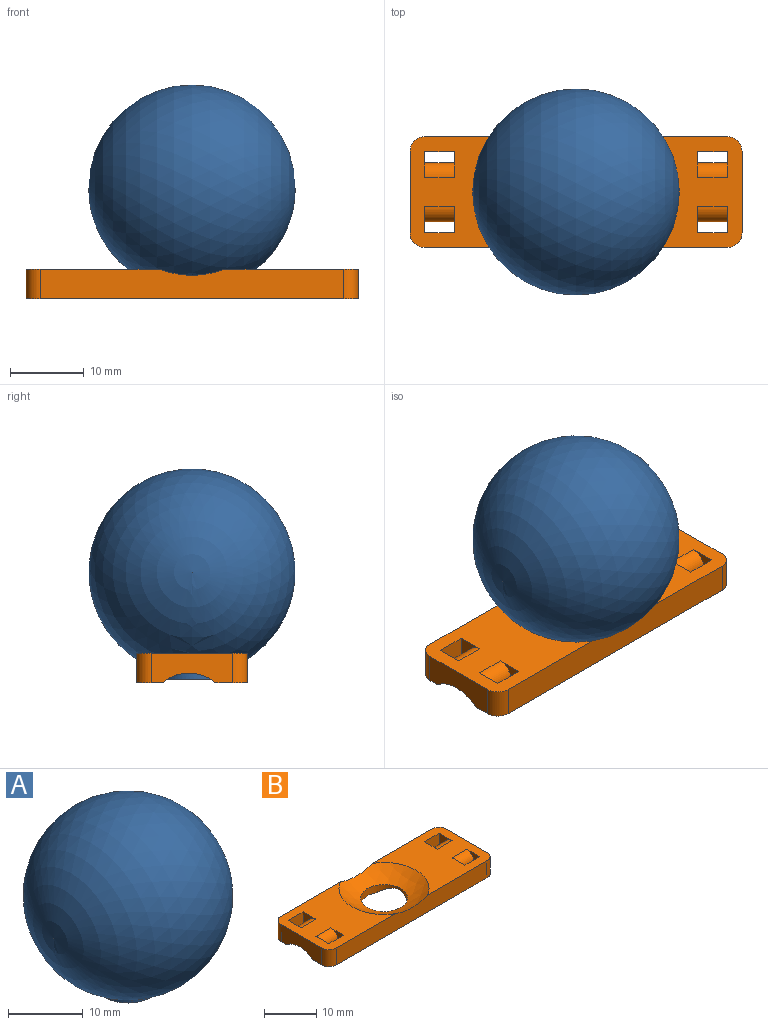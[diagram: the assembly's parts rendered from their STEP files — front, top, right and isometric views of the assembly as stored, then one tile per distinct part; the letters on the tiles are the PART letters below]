
ASSEMBLY  parts=2 mates=1
PART A: 3 faces, bbox 28x28x28.5 mm
  f0: sphere r=14mm, area 2402.1mm2, adj f1
  f1: cylinder r=4.35mm len=8.7mm, axis (0,0,1), area 32.6mm2, adj f0,f2
  f2: plane 8.7x8.7mm, normal (0,0,-1), area 59.4mm2, adj f1
PART B: 36 faces, bbox 45x15.8x5.9 mm
  f0: plane 45x4.26mm, normal (0,0,-1), area 172.5mm2, adj f1,f6,f7,f9,f14,f15,f16,f17
  f1: plane 11x4mm, normal (-1,0,0), area 37.5mm2, adj f0,f2,f3,f32,f33,f34
  f2: plane 18.17x15mm, normal (0,0,1), area 196.8mm2, adj f1,f5,f6,f8,f18,f19,f20,f22
  f3: plane 45x3.43mm, normal (0,0,-1), area 139.9mm2, adj f1,f7,f8,f9,f11,f12,f13,f22
  f4: plane 18.17x15mm, normal (0,0,1), area 196.8mm2, adj f5,f6,f7,f8,f11,f12,f13,f14
  f5: sphere r=14mm, area 181.8mm2, adj f2,f4,f6,f8,f9
  f6: plane 41x4mm, normal (0,-1,0), area 159.2mm2, adj f0,f2,f4,f5,f30,f33
  f7: plane 11x4mm, normal (1,0,0), area 37.5mm2, adj f0,f3,f4,f30,f31,f35
  f8: plane 41x4mm, normal (0,1,0), area 159.2mm2, adj f2,f3,f4,f5,f31,f32
  f9: cylinder r=4.5mm len=9mm, axis (0,0,1), area 35mm2, adj f0,f3,f5,f34,f35
  f10: plane 4x1.94mm, normal (0,1,0), area 7.8mm2, adj f11,f13,f29,f35
  f11: plane 4x3.5mm, normal (1,0,0), area 6.9mm2, adj f3,f4,f10,f12,f29,f35
  f12: plane 4x4mm, normal (0,-1,0), area 16mm2, adj f3,f4,f11,f13
  f13: plane 4x3.5mm, normal (-1,0,0), area 6.9mm2, adj f3,f4,f10,f12,f29,f35
  f14: plane 4x3.5mm, normal (1,0,0), area 6.9mm2, adj f0,f4,f15,f17,f28
  f15: plane 4x2mm, normal (0,-1,0), area 8mm2, adj f0,f14,f16,f28
  f16: plane 4x3.5mm, normal (-1,0,0), area 6.9mm2, adj f0,f4,f15,f17,f28
  f17: plane 4x4mm, normal (0,1,0), area 16mm2, adj f0,f4,f14,f16
  f18: plane 4x3.5mm, normal (-1,0,0), area 6.9mm2, adj f0,f2,f19,f21,f27
  f19: plane 4x4mm, normal (0,1,0), area 16mm2, adj f0,f2,f18,f20
  f20: plane 4x3.5mm, normal (1,0,0), area 6.9mm2, adj f0,f2,f19,f21,f27
  f21: plane 4x2mm, normal (0,-1,0), area 8mm2, adj f0,f18,f20,f27
  f22: plane 4x3.5mm, normal (-1,0,0), area 6.9mm2, adj f2,f3,f23,f25,f26,f34
  f23: plane 4x1.94mm, normal (0,1,0), area 7.8mm2, adj f22,f24,f26,f34
  f24: plane 4x3.5mm, normal (1,0,0), area 6.9mm2, adj f2,f3,f23,f25,f26,f34
  f25: plane 4x4mm, normal (0,-1,0), area 16mm2, adj f2,f3,f22,f24
  f26: cylinder r=2mm len=4mm, axis (-1,0,0), area 12.6mm2, adj f2,f22,f23,f24
  f27: cylinder r=2mm len=4mm, axis (1,0,0), area 12.6mm2, adj f2,f18,f20,f21
  f28: cylinder r=2mm len=4mm, axis (1,0,0), area 12.6mm2, adj f4,f14,f15,f16
  f29: cylinder r=2mm len=4mm, axis (-1,0,0), area 12.6mm2, adj f4,f10,f11,f13
  f30: cylinder r=2mm len=4mm, axis (0,0,-1), area 12.6mm2, adj f0,f4,f6,f7
  f31: cylinder r=2mm len=4mm, axis (0,0,1), area 12.6mm2, adj f3,f4,f7,f8
  f32: cylinder r=2mm len=4mm, axis (0,0,-1), area 12.6mm2, adj f1,f2,f3,f8
  f33: cylinder r=2mm len=4mm, axis (0,0,1), area 12.6mm2, adj f0,f1,f2,f6
  f34: cylinder r=5.8mm len=20.59mm, axis (-1,0,0), area 147.1mm2, adj f0,f1,f3,f9,f22,f23,f24
  f35: cylinder r=5.8mm len=20.59mm, axis (-1,0,0), area 147.2mm2, adj f0,f3,f7,f9,f10,f11,f13
PLACE A t=(-0.79,-9.04,-1.88)mm
PLACE B t=(-0.79,-9.04,-12.88)mm fixed
MATE ball A.f1 <-> B.f9  axis (0,0,1) through (-0.79,-9.04,-1.88)mm
